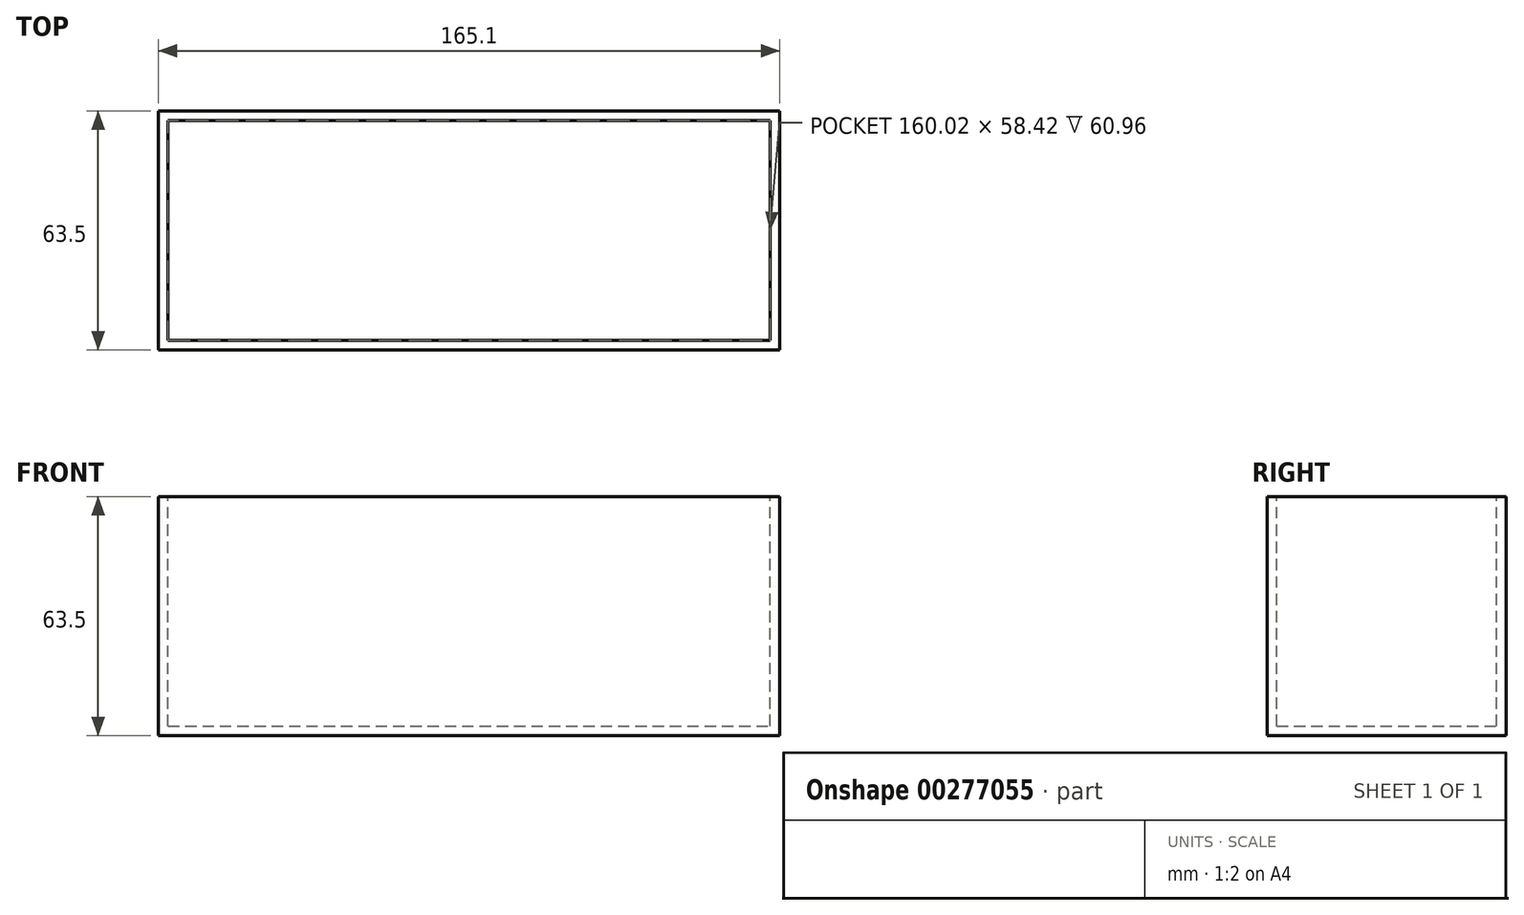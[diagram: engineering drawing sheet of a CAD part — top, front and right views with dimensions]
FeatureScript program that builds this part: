
annotation { "Feature Type Name" : "Feature", "Feature Type Description" : "" }
export const myFeature = defineFeature(function(context is Context, id is Id, definition is map)
    precondition{}
    {
        {
            var Q0;
            Q0=qCreatedBy(makeId("Front.planeOp"),FACE);
            var sketch = newSketch(context, id + "F0", { "sketchPlane" : qUnion([Q0])});
            skLineSegment(sketch, "E0.bottom", {"start": v(-82.55, -31.75) * mm, "end": v(82.55, -31.75) * mm});
            skLineSegment(sketch, "E0.top", {"start": v(-82.55, 31.75) * mm, "end": v(82.55, 31.75) * mm});
            skLineSegment(sketch, "E0.left", {"start": v(-82.55, -31.75) * mm, "end": v(-82.55, 31.75) * mm});
            skLineSegment(sketch, "E0.right", {"start": v(82.55, -31.75) * mm, "end": v(82.55, 31.75) * mm});
            skPoint(sketch, "E0.middle", {"position": v(0, 0) * mm});
            skSolve(sketch);
        }
        {
            var Q0;
            Q0=makeQuery(id+"F0.imprint","IMPRINT",FACE,{"disambiguationData":[TD([[makeQuery(id+"F0.imprint","IMPRINT",EDGE,{"derivedFrom":sQuery(id+"F0.wireOp",EDGE,"E0.bottom")}),1.0]])]});
            extrude(context, id + "F1", {"entities" : qUnion([Q0]), "endBound" : BoundingType.SYMMETRIC, "depth" : 63.5 * mm});
        }
        {
            var Q0;
            Q0=makeQuery(id+"F1.opExtrude","SWEPT_FACE",FACE,{"disambiguationData":[OSD([sQuery(id+"F0.wireOp",EDGE,"E0.top")])]});
            shell(context, id + "F2", {"entities" : qUnion([Q0]), "thickness" : 2.54 * mm});
        }
    });
